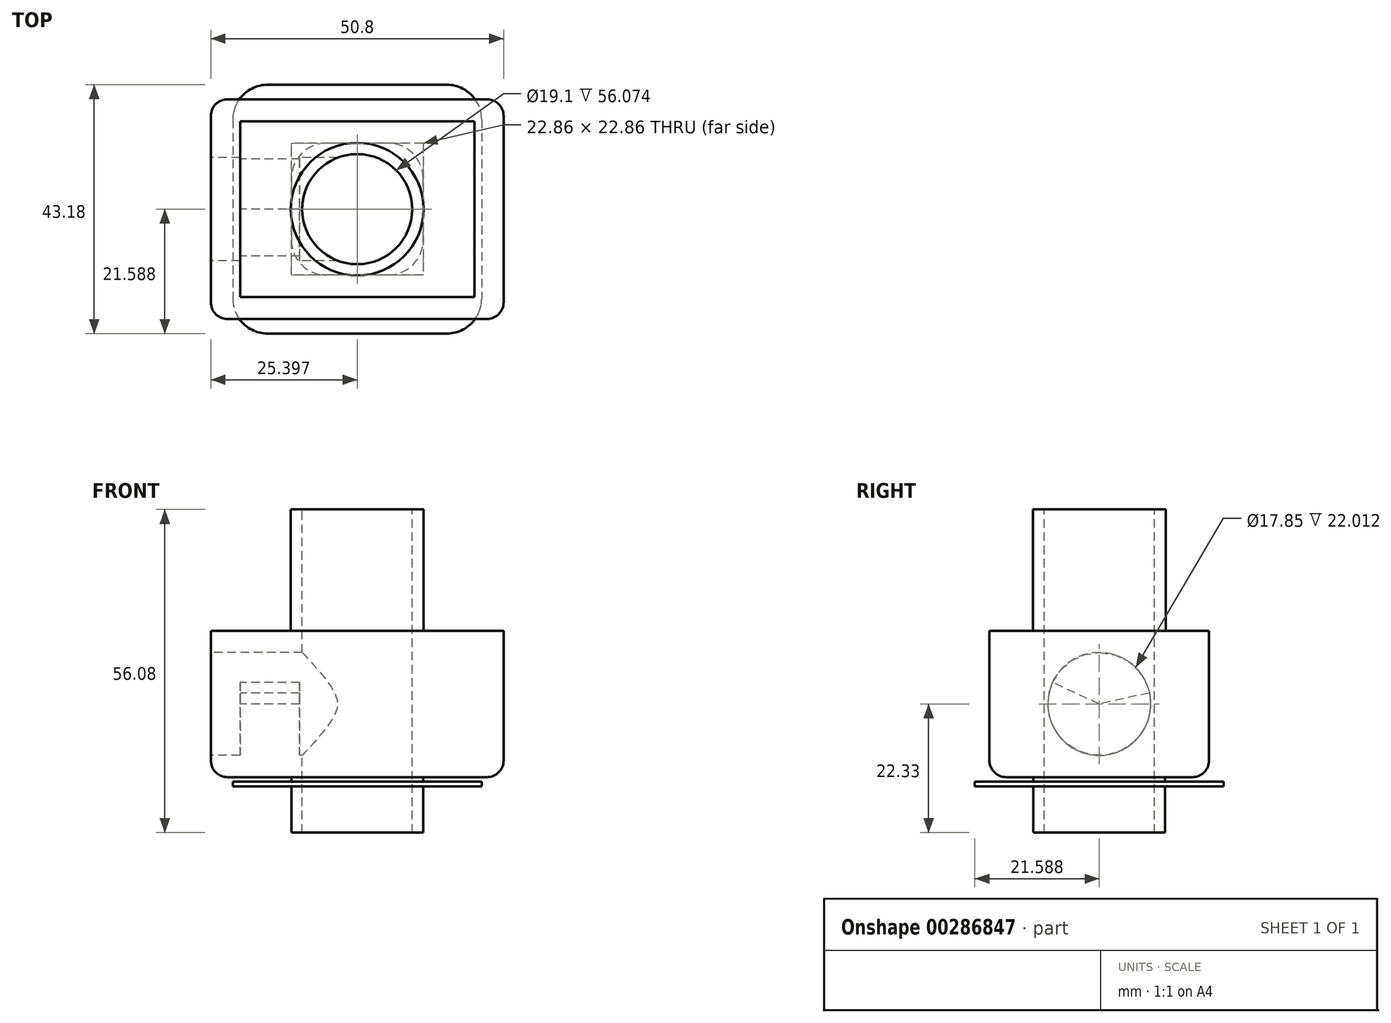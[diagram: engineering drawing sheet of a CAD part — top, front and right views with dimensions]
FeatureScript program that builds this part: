
annotation { "Feature Type Name" : "Feature", "Feature Type Description" : "" }
export const myFeature = defineFeature(function(context is Context, id is Id, definition is map)
    precondition{}
    {
        {
            var Q0;
            Q0=qCreatedBy(makeId("Top.planeOp"),FACE);
            var sketch = newSketch(context, id + "F0", { "sketchPlane" : qUnion([Q0])});
            skLineSegment(sketch, "E0.bottom", {"start": v(-57.85, 17.93) * mm, "end": v(-7.05, 17.93) * mm});
            skLineSegment(sketch, "E0.top", {"start": v(-57.85, -20.17) * mm, "end": v(-7.05, -20.17) * mm});
            skLineSegment(sketch, "E0.left", {"start": v(-57.85, 17.93) * mm, "end": v(-57.85, -20.17) * mm});
            skLineSegment(sketch, "E0.right", {"start": v(-7.05, 17.93) * mm, "end": v(-7.05, -20.17) * mm});
            skSolve(sketch);
        }
        {
            var Q0;
            Q0 = qSketchRegion(id + "F0", true);
            extrude(context, id + "F1", {"entities" : qUnion([Q0]), "depth" : 25.4 * mm});
        }
        {
            var Q0;
            Q0=makeQuery(id+"F1.opExtrude","CAP_FACE",FACE,{"disambiguationData":[OSD([sQuery(id+"F0.wireOp",EDGE,"E0.bottom"),sQuery(id+"F0.wireOp",EDGE,"E0.top"),sQuery(id+"F0.wireOp",EDGE,"E0.left"),sQuery(id+"F0.wireOp",EDGE,"E0.right")])],"isStart":false});
            var sketch = newSketch(context, id + "F2", { "sketchPlane" : qUnion([Q0])});
            skLineSegment(sketch, "E1.bottom", {"start": v(-52.77, -16.36) * mm, "end": v(-12.13, -16.36) * mm});
            skLineSegment(sketch, "E1.top", {"start": v(-52.77, 14.12) * mm, "end": v(-12.13, 14.12) * mm});
            skLineSegment(sketch, "E1.left", {"start": v(-52.77, -16.36) * mm, "end": v(-52.77, 14.12) * mm});
            skLineSegment(sketch, "E1.right", {"start": v(-12.13, -16.36) * mm, "end": v(-12.13, 14.12) * mm});
            skSolve(sketch);
        }
        {
            var Q0;
            Q0 = qSketchRegion(id + "F2", true);
            extrude(context, id + "F3", {"entities" : qUnion([Q0]), "operationType" : NewBodyOperationType.REMOVE, "oppositeDirection" : true, "depth" : 7 / 203.2 * mm});
        }
        {
            var Q0;
            Q0=makeQuery(id+"F3.boolean.opBoolean","COPY",FACE,{"derivedFrom":makeQuery(id+"F3.opExtrude","CAP_FACE",FACE,{"disambiguationData":[OSD([sQuery(id+"F2.wireOp",EDGE,"E1.bottom"),sQuery(id+"F2.wireOp",EDGE,"E1.top"),sQuery(id+"F2.wireOp",EDGE,"E1.left"),sQuery(id+"F2.wireOp",EDGE,"E1.right")])],"isStart":false})});
            var sketch = newSketch(context, id + "F4", { "sketchPlane" : qUnion([Q0])});
            skCircle(sketch, "E2", {"center": v(-32.45, -1.12) * mm, "radius": 9.55 * mm});
            skPoint(sketch, "E2.centerSnap0", {"position": v(-32.45, 14.12) * mm});
            skPoint(sketch, "E2.centerSnap1", {"position": v(-52.77, -1.12) * mm});
            skSolve(sketch);
        }
        {
            var Q0;
            Q0 = qSketchRegion(id + "F4", true);
            extrude(context, id + "F5", {"entities" : qUnion([Q0]), "operationType" : NewBodyOperationType.REMOVE, "oppositeDirection" : true, "depth" : 25.4 * mm});
        }
        {
            var Q0;
            Q0=makeQuery(id+"F1.opExtrude","SWEPT_FACE",FACE,{"disambiguationData":[OSD([sQuery(id+"F0.wireOp",EDGE,"E0.left")])]});
            var sketch = newSketch(context, id + "F6", { "sketchPlane" : qUnion([Q0])});
            skCircle(sketch, "E3", {"center": v(1.12, 12.7) * mm, "radius": 8.93 * mm});
            skSolve(sketch);
        }
        {
            var Q0;
            Q0 = qSketchRegion(id + "F6", true);
            extrude(context, id + "F7", {"entities" : qUnion([Q0]), "operationType" : NewBodyOperationType.REMOVE, "oppositeDirection" : true, "depth" : 25.4 * mm});
        }
        {
            var Q0;
            Q0=makeQuery(id+"F3.boolean.opBoolean","COPY",FACE,{"derivedFrom":makeQuery(id+"F3.opExtrude","SWEPT_FACE",FACE,{"disambiguationData":[OSD([sQuery(id+"F2.wireOp",EDGE,"E1.left")])]})});
            var sketch = newSketch(context, id + "F8", { "sketchPlane" : qUnion([Q0])});
            skCircle(sketch, "E4", {"center": v(-1.12, 12.7) * mm, "radius": 10.93 * mm});
            skLineSegment(sketch, "E5", {"start": v(9.55, 15.04) * mm, "end": v(-1.12, 12.7) * mm});
            skLineSegment(sketch, "E6", {"start": v(-1.12, 12.7) * mm, "end": v(-11.05, 17.26) * mm});
            skSolve(sketch);
        }
        {
            var Q0;
            {var subQ0=sQuery(id+"F8.wireOp",EDGE,"E6");var subQ1=sQuery(id+"F8.wireOp",EDGE,"E4");var subQ2=makeQuery(id+"F8.imprint","INTERSECT",VERTEX,{"derivedFrom":[subQ1,subQ0]});Q0=makeQuery(id+"F8.imprint","IMPRINT",FACE,{"disambiguationData":[TD([[makeQuery(id+"F8.imprint","IMPRINT",EDGE,{"disambiguationData":[TD([[subQ2,-1.0]])],"derivedFrom":subQ1}),1.0]])]});}
            extrude(context, id + "F9", {"entities" : qUnion([Q0]), "operationType" : NewBodyOperationType.ADD, "depth" : 10.34 * mm});
        }
        {
            var Q0;
            Q0=makeQuery(id+"F3.boolean.opBoolean","COPY",FACE,{"derivedFrom":makeQuery(id+"F3.opExtrude","CAP_FACE",FACE,{"disambiguationData":[OSD([sQuery(id+"F2.wireOp",EDGE,"E1.bottom"),sQuery(id+"F2.wireOp",EDGE,"E1.top"),sQuery(id+"F2.wireOp",EDGE,"E1.left"),sQuery(id+"F2.wireOp",EDGE,"E1.right")])],"isStart":false})});
            var sketch = newSketch(context, id + "F10", { "sketchPlane" : qUnion([Q0])});
            skCircle(sketch, "E7", {"center": v(-32.45, -1.12) * mm, "radius": 11.51 * mm});
            skLineSegment(sketch, "E8", {"start": v(-40.6, -9.26) * mm, "end": v(-32.45, -1.12) * mm});
            skLineSegment(sketch, "E9", {"start": v(-32.45, -1.12) * mm, "end": v(-23.02, -7.73) * mm});
            skLineSegment(sketch, "E10", {"start": v(-23.02, -7.73) * mm, "end": v(-32.45, -1.12) * mm});
            skLineSegment(sketch, "E11", {"start": v(-32.45, -1.12) * mm, "end": v(-23.02, 5.48) * mm});
            skLineSegment(sketch, "E12", {"start": v(-23.02, 5.48) * mm, "end": v(-32.45, -1.12) * mm});
            skLineSegment(sketch, "E13", {"start": v(-32.45, -1.12) * mm, "end": v(-40.6, 7.02) * mm});
            skLineSegment(sketch, "E14", {"start": v(-32.45, -1.12) * mm, "end": v(-12.13, -1.12) * mm});
            skSolve(sketch);
        }
        {
            var Q0;
            {var subQ0=sQuery(id+"F10.wireOp",EDGE,"E12");var subQ1=sQuery(id+"F10.wireOp",EDGE,"E7");var subQ2=makeQuery(id+"F10.imprint","INTERSECT",VERTEX,{"derivedFrom":[subQ1,subQ0]});Q0=makeQuery(id+"F10.imprint","IMPRINT",FACE,{"disambiguationData":[TD([[makeQuery(id+"F10.imprint","IMPRINT",EDGE,{"disambiguationData":[TD([[subQ2,-1.0]])],"derivedFrom":subQ1}),1.0]])]});}
            var Q1;
            {var subQ0=sQuery(id+"F10.wireOp",EDGE,"E8");var subQ1=sQuery(id+"F10.wireOp",EDGE,"E7");var subQ2=makeQuery(id+"F10.imprint","INTERSECT",VERTEX,{"derivedFrom":[subQ1,subQ0]});Q1=makeQuery(id+"F10.imprint","IMPRINT",FACE,{"disambiguationData":[TD([[makeQuery(id+"F10.imprint","IMPRINT",EDGE,{"disambiguationData":[TD([[subQ2,-1.0]])],"derivedFrom":subQ1}),1.0]])]});}
            extrude(context, id + "F11", {"entities" : qUnion([Q0, Q1]), "operationType" : NewBodyOperationType.ADD, "depth" : 21.08 * mm});
        }
        {
            var Q0;
            Q0=makeQuery(id+"F1.opExtrude","CAP_FACE",FACE,{"disambiguationData":[OSD([sQuery(id+"F0.wireOp",EDGE,"E0.bottom"),sQuery(id+"F0.wireOp",EDGE,"E0.top"),sQuery(id+"F0.wireOp",EDGE,"E0.left"),sQuery(id+"F0.wireOp",EDGE,"E0.right")])],"isStart":true});
            var sketch = newSketch(context, id + "F12", { "sketchPlane" : qUnion([Q0])});
            skCircle(sketch, "E15", {"center": v(-32.45, 1.12) * mm, "radius": 10.72 * mm});
            skLineSegment(sketch, "E16.bottom", {"start": v(-21.02, 12.55) * mm, "end": v(-43.88, 12.55) * mm});
            skLineSegment(sketch, "E16.top", {"start": v(-21.02, -10.3) * mm, "end": v(-43.88, -10.3) * mm});
            skLineSegment(sketch, "E16.left", {"start": v(-21.02, 12.55) * mm, "end": v(-21.02, -10.3) * mm});
            skLineSegment(sketch, "E16.right", {"start": v(-43.88, 12.55) * mm, "end": v(-43.88, -10.3) * mm});
            skSolve(sketch);
        }
        {
            var Q0;
            Q0=makeQuery(id+"F12.imprint","IMPRINT",FACE,{"disambiguationData":[TD([[makeQuery(id+"F12.imprint","IMPRINT",EDGE,{"derivedFrom":sQuery(id+"F12.wireOp",EDGE,"E15")}),1.0]])]});
            var Q1;
            Q1=makeQuery(id+"F12.imprint","IMPRINT",FACE,{"disambiguationData":[TD([[makeQuery(id+"F12.imprint","IMPRINT",EDGE,{"derivedFrom":sQuery(id+"F12.wireOp",EDGE,"E15")}),-1.0]])]});
            extrude(context, id + "F13", {"entities" : qUnion([Q0, Q1]), "operationType" : NewBodyOperationType.ADD, "depth" : 9.63 * mm});
        }
        {
            var Q0;
            Q0=makeQuery(id+"F13.opExtrude","SWEPT_FACE",FACE,{"disambiguationData":[OSD([sQuery(id+"F12.wireOp",EDGE,"E16.top")])]});
            var sketch = newSketch(context, id + "F14", { "sketchPlane" : qUnion([Q0])});
            skLineSegment(sketch, "E17", {"start": v(21.02, -0.8) * mm, "end": v(43.88, -0.8) * mm});
            skLineSegment(sketch, "E18", {"start": v(21.02, -1.59) * mm, "end": v(43.88, -1.59) * mm});
            skSolve(sketch);
        }
        {
            var Q0;
            {var subQ0=sQuery(id+"F14.wireOp",EDGE,"E17");Q0=makeQuery(id+"F14.imprint","IMPRINT",FACE,{"disambiguationData":[TD([[makeQuery(id+"F14.imprint","IMPRINT",EDGE,{"derivedFrom":subQ0}),-1.0]])]});}
            extrude(context, id + "F15", {"entities" : qUnion([Q0]), "operationType" : NewBodyOperationType.ADD, "depth" : 10.16 * mm});
        }
        {
            var Q0;
            {var subQ0=sQuery(id+"F12.wireOp",EDGE,"E16.left");Q0=makeQuery(id+"F15.boolean.opBoolean","MERGE",FACE,{"derivedFrom":[makeQuery(id+"F13.opExtrude","SWEPT_FACE",FACE,{"disambiguationData":[OSD([subQ0])]}),makeQuery(id+"F15.opExtrude","SWEPT_FACE",FACE,{"disambiguationData":[OSD([sQuery(id+"F12.wireOp",EDGE,"E16.top"),subQ0])]})]});}
            var sketch = newSketch(context, id + "F16", { "sketchPlane" : qUnion([Q0])});
            skLineSegment(sketch, "E19", {"start": v(-12.55, -1.59) * mm, "end": v(10.3, -1.59) * mm});
            skLineSegment(sketch, "E20", {"start": v(-12.55, -0.8) * mm, "end": v(10.3, -0.8) * mm});
            skSolve(sketch);
        }
        {
            var Q0;
            {var subQ3=sQuery(id+"F16.wireOp",EDGE,"E19");Q0=makeQuery(id+"F16.imprint","IMPRINT",FACE,{"disambiguationData":[TD([[makeQuery(id+"F16.imprint","IMPRINT",EDGE,{"derivedFrom":subQ3}),1.0]])]});}
            var Q1;
            Q1 = qSketchRegion(id + "FxDFH36QrSwnas9_1", true);
            extrude(context, id + "F17", {"entities" : qUnion([Q0, Q1]), "operationType" : NewBodyOperationType.ADD, "depth" : 10.16 * mm});
        }
        {
            var Q0;
            {var subQ0=sQuery(id+"F12.wireOp",EDGE,"E16.bottom");Q0=makeQuery(id+"F17.boolean.opBoolean","MERGE",FACE,{"derivedFrom":[makeQuery(id+"F13.opExtrude","SWEPT_FACE",FACE,{"disambiguationData":[OSD([subQ0])]}),makeQuery(id+"F17.opExtrude","SWEPT_FACE",FACE,{"disambiguationData":[OSD([subQ0,sQuery(id+"F12.wireOp",EDGE,"E16.left")])]})]});}
            var sketch = newSketch(context, id + "F18", { "sketchPlane" : qUnion([Q0])});
            skLineSegment(sketch, "E21.bottom", {"start": v(-21.02, -0.8) * mm, "end": v(-43.88, -0.8) * mm});
            skLineSegment(sketch, "E21.top", {"start": v(-21.02, -1.59) * mm, "end": v(-43.88, -1.59) * mm});
            skLineSegment(sketch, "E21.left", {"start": v(-21.02, -0.8) * mm, "end": v(-21.02, -1.59) * mm});
            skLineSegment(sketch, "E21.right", {"start": v(-43.88, -0.8) * mm, "end": v(-43.88, -1.59) * mm});
            skSolve(sketch);
        }
        {
            var Q0;
            Q0=makeQuery(id+"F18.imprint","IMPRINT",FACE,{"disambiguationData":[TD([[makeQuery(id+"F18.imprint","IMPRINT",EDGE,{"derivedFrom":sQuery(id+"F18.wireOp",EDGE,"E21.left")}),1.0]])]});
            var Q1;
            Q1=makeQuery(id+"F18.imprint","IMPRINT",FACE,{"disambiguationData":[TD([[makeQuery(id+"F18.imprint","IMPRINT",EDGE,{"derivedFrom":sQuery(id+"F18.wireOp",EDGE,"E21.bottom")}),1.0]])]});
            extrude(context, id + "F19", {"entities" : qUnion([Q0, Q1]), "operationType" : NewBodyOperationType.ADD, "depth" : 10.16 * mm});
        }
        {
            var Q0;
            {var subQ0=sQuery(id+"F12.wireOp",EDGE,"E16.right");Q0=makeQuery(id+"F19.boolean.opBoolean","MERGE",FACE,{"derivedFrom":[makeQuery(id+"F15.boolean.opBoolean","MERGE",FACE,{"derivedFrom":[makeQuery(id+"F13.opExtrude","SWEPT_FACE",FACE,{"disambiguationData":[OSD([subQ0])]}),makeQuery(id+"F15.opExtrude","SWEPT_FACE",FACE,{"disambiguationData":[OSD([sQuery(id+"F12.wireOp",EDGE,"E16.top"),subQ0])]})]}),makeQuery(id+"F19.opExtrude","SWEPT_FACE",FACE,{"disambiguationData":[OSD([sQuery(id+"F18.wireOp",EDGE,"E21.right")])]})]});}
            var sketch = newSketch(context, id + "F20", { "sketchPlane" : qUnion([Q0])});
            skLineSegment(sketch, "E22.bottom", {"start": v(-10.3, -0.8) * mm, "end": v(12.55, -0.8) * mm});
            skLineSegment(sketch, "E22.top", {"start": v(-10.3, -1.59) * mm, "end": v(12.55, -1.59) * mm});
            skLineSegment(sketch, "E22.left", {"start": v(-10.3, -0.8) * mm, "end": v(-10.3, -1.59) * mm});
            skLineSegment(sketch, "E22.right", {"start": v(12.55, -0.8) * mm, "end": v(12.55, -1.59) * mm});
            skSolve(sketch);
        }
        {
            var Q0;
            Q0=makeQuery(id+"F20.imprint","IMPRINT",FACE,{"disambiguationData":[TD([[makeQuery(id+"F20.imprint","IMPRINT",EDGE,{"derivedFrom":sQuery(id+"F20.wireOp",EDGE,"E22.left")}),-1.0]])]});
            var Q1;
            Q1=makeQuery(id+"F20.imprint","IMPRINT",FACE,{"disambiguationData":[TD([[makeQuery(id+"F20.imprint","IMPRINT",EDGE,{"derivedFrom":sQuery(id+"F20.wireOp",EDGE,"E22.bottom")}),-1.0]])]});
            var Q2;
            Q2=makeQuery(id+"F20.imprint","IMPRINT",FACE,{"disambiguationData":[TD([[makeQuery(id+"F20.imprint","IMPRINT",EDGE,{"derivedFrom":sQuery(id+"F20.wireOp",EDGE,"E22.right")}),1.0]])]});
            extrude(context, id + "F21", {"entities" : qUnion([Q0, Q1, Q2]), "operationType" : NewBodyOperationType.ADD, "depth" : 10.16 * mm});
        }
        {
            var Q0;
            Q0=makeQuery(id+"F17.opExtrude","CAP_EDGE",EDGE,{"disambiguationData":[OSD([sQuery(id+"F12.wireOp",EDGE,"E16.top"),sQuery(id+"F12.wireOp",EDGE,"E16.left")])],"isStart":false});
            var Q1;
            Q1=makeQuery(id+"F21.opExtrude","CAP_EDGE",EDGE,{"disambiguationData":[OSD([sQuery(id+"F12.wireOp",EDGE,"E16.top"),sQuery(id+"F12.wireOp",EDGE,"E16.right")])],"isStart":false});
            var Q2;
            Q2=makeQuery(id+"F21.opExtrude","CAP_EDGE",EDGE,{"disambiguationData":[OSD([sQuery(id+"F18.wireOp",EDGE,"E21.right")])],"isStart":false});
            var Q3;
            Q3=makeQuery(id+"F19.opExtrude","CAP_EDGE",EDGE,{"disambiguationData":[OSD([sQuery(id+"F12.wireOp",EDGE,"E16.bottom"),sQuery(id+"F12.wireOp",EDGE,"E16.left")])],"isStart":false});
            var Q4;
            {var subQ0=sQuery(id+"F12.wireOp",EDGE,"E16.left");var subQ1=sQuery(id+"F12.wireOp",EDGE,"E16.bottom");var subQ2=sQuery(id+"F14.wireOp",EDGE,"E18");Q4=makeQuery(id+"F17.boolean.opBoolean","SPLIT",EDGE,{"disambiguationData":[TD([makeQuery(id+"F15.opExtrude","SWEPT_FACE",FACE,{"disambiguationData":[OSD([subQ2])]})])],"derivedFrom":makeQuery(id+"F13.opExtrude","SWEPT_EDGE",EDGE,{"disambiguationData":[OSD([subQ1,subQ0])]})});}
            var Q5;
            {var subQ0=sQuery(id+"F14.wireOp",EDGE,"E18");var subQ1=sQuery(id+"F12.wireOp",EDGE,"E16.right");var subQ4=sQuery(id+"F12.wireOp",EDGE,"E16.bottom");Q5=makeQuery(id+"F19.boolean.opBoolean","SPLIT",EDGE,{"disambiguationData":[TD([makeQuery(id+"F15.opExtrude","SWEPT_FACE",FACE,{"disambiguationData":[OSD([subQ0])]})])],"derivedFrom":makeQuery(id+"F13.opExtrude","SWEPT_EDGE",EDGE,{"disambiguationData":[OSD([subQ4,subQ1])]})});}
            var Q6;
            {var subQ0=sQuery(id+"F12.wireOp",EDGE,"E16.right");var subQ1=sQuery(id+"F12.wireOp",EDGE,"E16.top");Q6=makeQuery(id+"F15.boolean.opBoolean","SPLIT",EDGE,{"disambiguationData":[TD([makeQuery(id+"F15.opExtrude","SWEPT_FACE",FACE,{"disambiguationData":[OSD([sQuery(id+"F14.wireOp",EDGE,"E18")])]})])],"derivedFrom":makeQuery(id+"F13.opExtrude","SWEPT_EDGE",EDGE,{"disambiguationData":[OSD([subQ1,subQ0])]})});}
            var Q7;
            {var subQ0=sQuery(id+"F12.wireOp",EDGE,"E16.left");var subQ1=sQuery(id+"F12.wireOp",EDGE,"E16.top");Q7=makeQuery(id+"F15.boolean.opBoolean","SPLIT",EDGE,{"disambiguationData":[TD([makeQuery(id+"F15.opExtrude","SWEPT_FACE",FACE,{"disambiguationData":[OSD([sQuery(id+"F14.wireOp",EDGE,"E18")])]})])],"derivedFrom":makeQuery(id+"F13.opExtrude","SWEPT_EDGE",EDGE,{"disambiguationData":[OSD([subQ1,subQ0])]})});}
            fillet(context, id + "F22", {"entities" : qUnion([Q0, Q1, Q2, Q3, Q4, Q5, Q6, Q7]), "radius" : 6.07 * mm, "tangentPropagation" : true, "allowEdgeOverflow" : false});
        }
        {
            var Q0;
            Q0=makeQuery(id+"F1.opExtrude","CAP_EDGE",EDGE,{"disambiguationData":[OSD([sQuery(id+"F0.wireOp",EDGE,"E0.top")])],"isStart":true});
            var Q1;
            Q1=makeQuery(id+"F1.opExtrude","CAP_EDGE",EDGE,{"disambiguationData":[OSD([sQuery(id+"F0.wireOp",EDGE,"E0.left")])],"isStart":true});
            var Q2;
            Q2=makeQuery(id+"F1.opExtrude","SWEPT_EDGE",EDGE,{"disambiguationData":[OSD([sQuery(id+"F0.wireOp",EDGE,"E0.top"),sQuery(id+"F0.wireOp",EDGE,"E0.left")])]});
            var Q3;
            Q3=makeQuery(id+"F1.opExtrude","CAP_EDGE",EDGE,{"disambiguationData":[OSD([sQuery(id+"F0.wireOp",EDGE,"E0.right")])],"isStart":true});
            var Q4;
            Q4=makeQuery(id+"F1.opExtrude","SWEPT_EDGE",EDGE,{"disambiguationData":[OSD([sQuery(id+"F0.wireOp",EDGE,"E0.top"),sQuery(id+"F0.wireOp",EDGE,"E0.right")])]});
            var Q5;
            Q5=makeQuery(id+"F1.opExtrude","CAP_EDGE",EDGE,{"disambiguationData":[OSD([sQuery(id+"F0.wireOp",EDGE,"E0.bottom")])],"isStart":true});
            var Q6;
            Q6=makeQuery(id+"F1.opExtrude","SWEPT_EDGE",EDGE,{"disambiguationData":[OSD([sQuery(id+"F0.wireOp",EDGE,"E0.bottom"),sQuery(id+"F0.wireOp",EDGE,"E0.right")])]});
            var Q7;
            Q7=makeQuery(id+"F1.opExtrude","SWEPT_EDGE",EDGE,{"disambiguationData":[OSD([sQuery(id+"F0.wireOp",EDGE,"E0.bottom"),sQuery(id+"F0.wireOp",EDGE,"E0.left")])]});
            fillet(context, id + "F23", {"entities" : qUnion([Q0, Q1, Q2, Q3, Q4, Q5, Q6, Q7]), "radius" : 2.88 * mm, "tangentPropagation" : true, "allowEdgeOverflow" : false});
        }
    });
